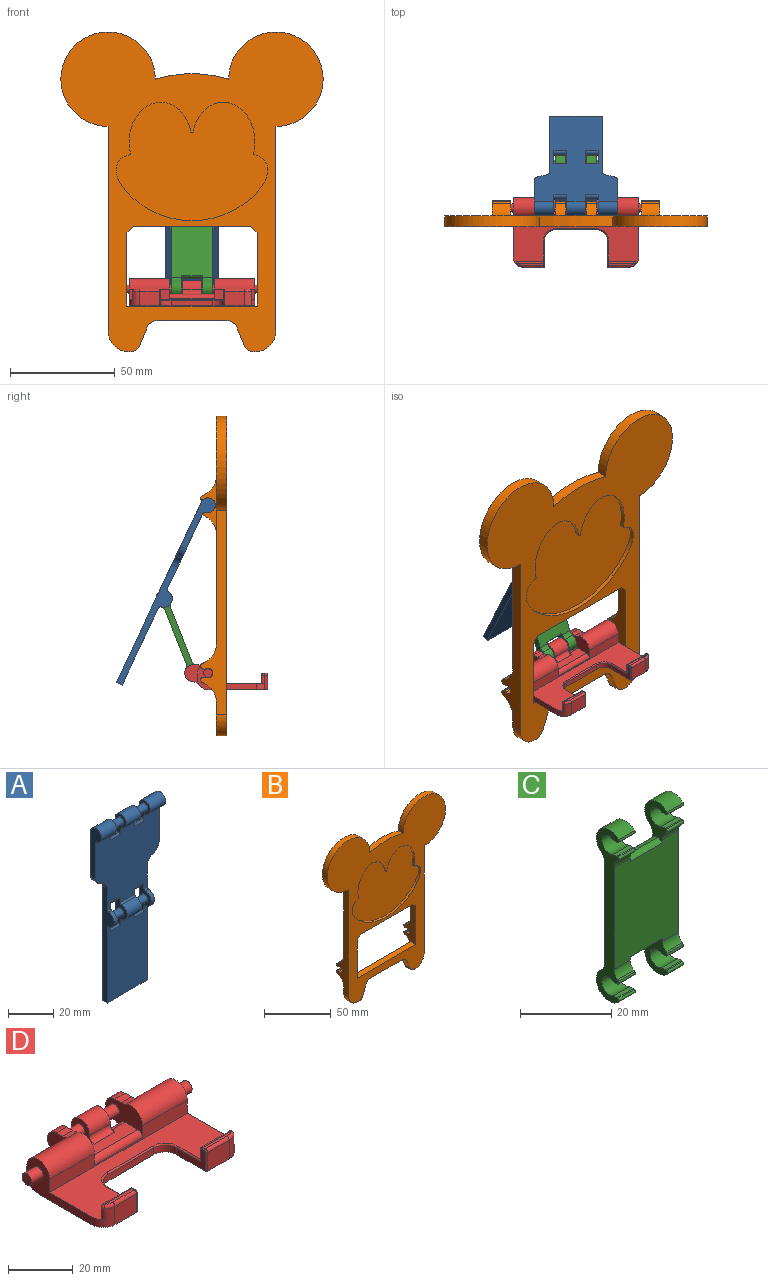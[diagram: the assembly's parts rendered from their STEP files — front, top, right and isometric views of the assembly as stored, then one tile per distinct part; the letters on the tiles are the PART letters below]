
ASSEMBLY  parts=4 mates=4
PART A: 57 faces, bbox 40x7.5x98.5 mm
  f0: cylinder r=4mm len=9mm, axis (-1,0,0), area 105.9mm2, adj f1,f2,f33,f40
  f1: cylinder r=1mm len=9mm, axis (-1,0,0), area 13.2mm2, adj f0,f12,f33,f40
  f2: cylinder r=1mm len=9mm, axis (-1,0,0), area 13.2mm2, adj f0,f9,f33,f40
  f3: plane 95x40mm, normal (0,1,0), area 2523.8mm2, adj f5,f11,f13,f14,f15,f16,f17,f18
  f4: cylinder r=2mm len=9mm, axis (-1,0,0), area 23.3mm2, adj f9,f11,f29,f36
  f5: cylinder r=3.5mm len=9.5mm, axis (-1,0,0), area 147.5mm2, adj f3,f14,f24,f35
  f6: cylinder r=4mm len=7.96mm, axis (-1,0,0), area 23.5mm2, adj f7,f8,f16,f39
  f7: cylinder r=1mm len=2mm, axis (-1,0,0), area 2.9mm2, adj f6,f12,f16,f39
  f8: cylinder r=1mm len=2mm, axis (-1,0,0), area 2.9mm2, adj f6,f9,f16,f39
  f9: plane 40x39.08mm, normal (0,-1,0), area 1254.7mm2, adj f2,f4,f8,f10,f14,f15,f16,f17
  f10: cylinder r=2mm len=9.5mm, axis (-1,0,0), area 24.6mm2, adj f9,f15,f22,f28
  f11: cylinder r=3.5mm len=9mm, axis (-1,0,0), area 139.7mm2, adj f3,f4,f29,f36
  f12: plane 40.68x25mm, normal (0,-1,0), area 982.3mm2, adj f1,f7,f13,f16,f18,f25,f32,f33
  f13: plane 25x3mm, normal (0,0,-1), area 75mm2, adj f3,f12,f16,f18
  f14: plane 26.82x7mm, normal (-1,0,0), area 101.1mm2, adj f3,f5,f9,f21,f24
  f15: plane 26.82x7mm, normal (1,0,0), area 101.1mm2, adj f3,f9,f10,f20,f22
  f16: plane 62x7.5mm, normal (-1,0,0), area 215.5mm2, adj f3,f6,f7,f8,f9,f12,f13,f17
  f17: cylinder r=5mm len=4.84mm, axis (0,1,0), area 19.8mm2, adj f3,f9,f16,f21
  f18: plane 62x7.5mm, normal (1,0,0), area 215.5mm2, adj f3,f9,f12,f13,f19,f23,f25,f26
  f19: cylinder r=5mm len=4.84mm, axis (0,1,0), area 19.8mm2, adj f3,f9,f18,f20
  f20: cylinder r=5mm len=4.84mm, axis (0,1,0), area 19.8mm2, adj f3,f9,f15,f19
  f21: cylinder r=5mm len=4.84mm, axis (0,1,0), area 19.8mm2, adj f3,f9,f14,f17
  f22: cylinder r=3.5mm len=9.5mm, axis (-1,0,0), area 147.5mm2, adj f3,f10,f15,f28
  f23: cylinder r=4mm len=7.96mm, axis (-1,0,0), area 23.5mm2, adj f18,f25,f26,f32
  f24: cylinder r=2mm len=9.5mm, axis (-1,0,0), area 24.6mm2, adj f5,f9,f14,f35
  f25: cylinder r=1mm len=2mm, axis (-1,0,0), area 2.9mm2, adj f12,f18,f23,f32
  f26: cylinder r=1mm len=2mm, axis (-1,0,0), area 2.9mm2, adj f9,f18,f23,f32
  f27: cylinder r=7mm len=6mm, axis (-1,0,0), area 5.4mm2, adj f28,f29,f55,f56
  f28: plane 11.36x7mm, normal (-1,0,0), area 39.2mm2, adj f3,f9,f10,f22,f27,f42,f55,f56
  f29: plane 11.36x7mm, normal (1,0,0), area 39.2mm2, adj f3,f4,f9,f11,f27,f42,f55,f56
  f30: cylinder r=7mm len=6mm, axis (-1,0,0), area 5.4mm2, adj f32,f33,f51,f53
  f31: cylinder r=7mm len=6mm, axis (-1,0,0), area 5.4mm2, adj f32,f33,f52,f54
  f32: plane 15.72x7.5mm, normal (-1,0,0), area 58.1mm2, adj f3,f9,f12,f23,f25,f26,f30,f31
  f33: plane 15.72x7.5mm, normal (1,0,0), area 58.1mm2, adj f0,f1,f2,f3,f9,f12,f30,f31
  f34: cylinder r=7mm len=6mm, axis (1,0,0), area 5.4mm2, adj f35,f36,f49,f50
  f35: plane 11.36x7mm, normal (1,0,0), area 39.2mm2, adj f3,f5,f9,f24,f34,f41,f49,f50
  f36: plane 11.36x7mm, normal (-1,0,0), area 39.2mm2, adj f3,f4,f9,f11,f34,f41,f49,f50
  f37: cylinder r=7mm len=6mm, axis (1,0,0), area 5.4mm2, adj f39,f40,f45,f47
  f38: cylinder r=7mm len=6mm, axis (1,0,0), area 5.4mm2, adj f39,f40,f46,f48
  f39: plane 15.72x7.5mm, normal (1,0,0), area 58.1mm2, adj f3,f6,f7,f8,f9,f12,f37,f38
  f40: plane 15.72x7.5mm, normal (-1,0,0), area 58.1mm2, adj f0,f1,f2,f3,f9,f12,f37,f38
  f41: cylinder r=2mm len=6mm, axis (-1,0,0), area 75.4mm2, adj f35,f36
  f42: cylinder r=2mm len=6mm, axis (-1,0,0), area 75.4mm2, adj f28,f29
  f43: cylinder r=2mm len=6mm, axis (-1,0,0), area 75.4mm2, adj f39,f40
  f44: cylinder r=2mm len=6mm, axis (-1,0,0), area 75.4mm2, adj f32,f33
  f45: cylinder r=1mm len=6mm, axis (1,0,0), area 8.3mm2, adj f9,f37,f39,f40
  f46: cylinder r=1mm len=6mm, axis (1,0,0), area 8.3mm2, adj f12,f38,f39,f40
  f47: cylinder r=1mm len=6mm, axis (1,0,0), area 11.3mm2, adj f3,f37,f39,f40
  f48: cylinder r=1mm len=6mm, axis (1,0,0), area 11.3mm2, adj f3,f38,f39,f40
  f49: cylinder r=1mm len=6mm, axis (1,0,0), area 8.3mm2, adj f9,f34,f35,f36
  f50: cylinder r=1mm len=6mm, axis (1,0,0), area 11.3mm2, adj f3,f34,f35,f36
  f51: cylinder r=1mm len=6mm, axis (-1,0,0), area 8.3mm2, adj f9,f30,f32,f33
  f52: cylinder r=1mm len=6mm, axis (-1,0,0), area 8.3mm2, adj f12,f31,f32,f33
  f53: cylinder r=1mm len=6mm, axis (-1,0,0), area 11.3mm2, adj f3,f30,f32,f33
  f54: cylinder r=1mm len=6mm, axis (-1,0,0), area 11.3mm2, adj f3,f31,f32,f33
  f55: cylinder r=1mm len=6mm, axis (-1,0,0), area 8.3mm2, adj f9,f27,f28,f29
  f56: cylinder r=1mm len=6mm, axis (-1,0,0), area 11.3mm2, adj f3,f27,f28,f29
PART B: 90 faces, bbox 125x12.5x152.5 mm
  f0: plane 80x21.9mm, normal (0,1,0), area 909.3mm2, adj f3,f7,f8,f9,f10,f11,f12,f13
  f1: plane 152.5x125mm, normal (0,-1,0), area 6689.7mm2, adj f3,f4,f5,f6,f7,f8,f9,f10
  f2: plane 125x108.48mm, normal (0,1,0), area 8063mm2, adj f4,f5,f6,f7,f9,f19,f20,f26
  f3: plane 5x0.45mm, normal (0,0,-1), area 2.2mm2, adj f0,f1,f10,f18
  f4: cylinder r=22.5mm len=45mm, axis (0,-1,0), area 530.1mm2, adj f1,f2,f5,f9
  f5: cylinder r=60mm len=35mm, axis (0,-1,0), area 177.6mm2, adj f1,f2,f4,f6
  f6: cylinder r=22.5mm len=45mm, axis (0,-1,0), area 530.1mm2, adj f1,f2,f5,f7
  f7: plane 97.5x12.49mm, normal (-1,0,0), area 566.5mm2, adj f0,f1,f2,f6,f10,f40,f41,f42
  f8: plane 5x0.45mm, normal (0,0,-1), area 2.2mm2, adj f0,f1,f11,f17
  f9: plane 97.5x12.49mm, normal (1,0,0), area 566.5mm2, adj f0,f1,f2,f4,f11,f27,f28,f29
  f10: cylinder r=10mm len=10mm, axis (0,-1,0), area 78.5mm2, adj f0,f1,f3,f7
  f11: cylinder r=10mm len=10mm, axis (0,1,0), area 78.5mm2, adj f0,f1,f8,f9
  f12: plane 33.32x5mm, normal (0,0,-1), area 166.6mm2, adj f0,f1,f15,f16
  f13: plane 8.83x5mm, normal (-0.92,0,-0.38), area 47.8mm2, adj f0,f1,f16,f17
  f14: plane 8.83x5mm, normal (0.92,0,-0.38), area 47.8mm2, adj f0,f1,f15,f18
  f15: cylinder r=5mm len=5mm, axis (0,1,0), area 29.5mm2, adj f0,f1,f12,f14
  f16: cylinder r=5mm len=5mm, axis (0,-1,0), area 29.5mm2, adj f0,f1,f12,f13
  f17: cylinder r=5mm len=5mm, axis (0,1,0), area 29.5mm2, adj f0,f1,f8,f13
  f18: cylinder r=5mm len=5mm, axis (0,-1,0), area 29.5mm2, adj f0,f1,f3,f14
  f19: plane 28.04x7.49mm, normal (1,0,0), area 79mm2, adj f2,f21,f22,f23,f24,f25,f53,f54
  f20: plane 28.04x7.49mm, normal (-1,0,0), area 79mm2, adj f2,f21,f22,f23,f24,f25,f53,f54
  f21: cylinder r=5.25mm len=5mm, axis (-1,0,0), area 4.5mm2, adj f19,f20,f56,f67
  f22: plane 5x0.31mm, normal (0,0,1), area 1.5mm2, adj f19,f20,f55,f77
  f23: cylinder r=2.3mm len=5mm, axis (-1,0,0), area 46.1mm2, adj f19,f20,f77,f78
  f24: plane 5x0.31mm, normal (0,0,-1), area 1.5mm2, adj f19,f20,f54,f78
  f25: cylinder r=5.25mm len=5mm, axis (-1,0,0), area 4.5mm2, adj f19,f20,f53,f68
  f26: plane 41.02x12.49mm, normal (-1,0,0), area 254.5mm2, adj f0,f1,f2,f27,f28,f29,f30,f31
  f27: cylinder r=5.25mm len=9mm, axis (-1,0,0), area 8mm2, adj f9,f26,f48,f65
  f28: plane 9x0.31mm, normal (0,0,1), area 2.8mm2, adj f9,f26,f47,f76
  f29: cylinder r=2.3mm len=9mm, axis (-1,0,0), area 83mm2, adj f9,f26,f75,f76
  f30: plane 9x0.31mm, normal (0,0,-1), area 2.8mm2, adj f9,f26,f46,f75
  f31: cylinder r=5.25mm len=9mm, axis (-1,0,0), area 8mm2, adj f9,f26,f45,f66
  f32: plane 28.04x7.49mm, normal (-1,0,0), area 79mm2, adj f2,f34,f35,f36,f37,f38,f57,f58
  f33: plane 28.04x7.49mm, normal (1,0,0), area 79mm2, adj f2,f34,f35,f36,f37,f38,f57,f58
  f34: cylinder r=5.25mm len=5mm, axis (1,0,0), area 4.5mm2, adj f32,f33,f58,f63
  f35: plane 5x0.31mm, normal (0,0,-1), area 1.5mm2, adj f32,f33,f57,f74
  f36: cylinder r=2.3mm len=5mm, axis (1,0,0), area 46.1mm2, adj f32,f33,f73,f74
  f37: plane 5x0.31mm, normal (0,0,1), area 1.5mm2, adj f32,f33,f60,f73
  f38: cylinder r=5.25mm len=5mm, axis (1,0,0), area 4.5mm2, adj f32,f33,f59,f64
  f39: plane 41.02x12.49mm, normal (1,0,0), area 254.5mm2, adj f0,f1,f2,f40,f41,f42,f43,f44
  f40: cylinder r=5.25mm len=9mm, axis (1,0,0), area 8mm2, adj f7,f39,f50,f61
  f41: plane 9x0.31mm, normal (0,0,-1), area 2.8mm2, adj f7,f39,f49,f71
  f42: cylinder r=2.3mm len=9mm, axis (1,0,0), area 83mm2, adj f7,f39,f71,f72
  f43: plane 9x0.31mm, normal (0,0,1), area 2.8mm2, adj f7,f39,f52,f72
  f44: cylinder r=5.25mm len=9mm, axis (1,0,0), area 8mm2, adj f7,f39,f51,f62
  f45: cylinder r=1.4mm len=9mm, axis (-1,0,0), area 17.3mm2, adj f9,f26,f31,f46
  f46: cylinder r=1.4mm len=9mm, axis (-1,0,0), area 14.4mm2, adj f9,f26,f30,f45
  f47: cylinder r=1.4mm len=9mm, axis (-1,0,0), area 14.4mm2, adj f9,f26,f28,f48
  f48: cylinder r=1.4mm len=9mm, axis (-1,0,0), area 17.3mm2, adj f9,f26,f27,f47
  f49: cylinder r=1.4mm len=9mm, axis (1,0,0), area 14.4mm2, adj f7,f39,f41,f50
  f50: cylinder r=1.4mm len=9mm, axis (1,0,0), area 17.3mm2, adj f7,f39,f40,f49
  f51: cylinder r=1.4mm len=9mm, axis (1,0,0), area 17.3mm2, adj f7,f39,f44,f52
  f52: cylinder r=1.4mm len=9mm, axis (1,0,0), area 14.4mm2, adj f7,f39,f43,f51
  f53: cylinder r=1.4mm len=5mm, axis (-1,0,0), area 9.6mm2, adj f19,f20,f25,f54
  f54: cylinder r=1.4mm len=5mm, axis (1,0,0), area 8mm2, adj f19,f20,f24,f53
  f55: cylinder r=1.4mm len=5mm, axis (-1,0,0), area 8mm2, adj f19,f20,f22,f56
  f56: cylinder r=1.4mm len=5mm, axis (-1,0,0), area 9.6mm2, adj f19,f20,f21,f55
  f57: cylinder r=1.4mm len=5mm, axis (-1,0,0), area 8mm2, adj f32,f33,f35,f58
  f58: cylinder r=1.4mm len=5mm, axis (1,0,0), area 9.6mm2, adj f32,f33,f34,f57
  f59: cylinder r=1.4mm len=5mm, axis (1,0,0), area 9.6mm2, adj f32,f33,f38,f60
  f60: cylinder r=1.4mm len=5mm, axis (1,0,0), area 8mm2, adj f32,f33,f37,f59
  f61: cylinder r=10mm len=9.19mm, axis (1,0,0), area 105mm2, adj f2,f7,f39,f40
  f62: cylinder r=10mm len=9.19mm, axis (1,0,0), area 105mm2, adj f0,f7,f39,f44
  f63: cylinder r=10mm len=9.19mm, axis (1,0,0), area 58.3mm2, adj f2,f32,f33,f34
  f64: cylinder r=10mm len=9.19mm, axis (1,0,0), area 58.3mm2, adj f2,f32,f33,f38
  f65: cylinder r=10mm len=9.19mm, axis (-1,0,0), area 105mm2, adj f0,f9,f26,f27
  f66: cylinder r=10mm len=9.19mm, axis (-1,0,0), area 105mm2, adj f2,f9,f26,f31
  f67: cylinder r=10mm len=9.19mm, axis (-1,0,0), area 58.3mm2, adj f2,f19,f20,f21
  f68: cylinder r=10mm len=9.19mm, axis (-1,0,0), area 58.3mm2, adj f2,f19,f20,f25
  f69: plane 56x5mm, normal (0,0,-1), area 280mm2, adj f1,f2,f79,f80
  f70: plane 62x5mm, normal (0,0,1), area 310mm2, adj f0,f1,f26,f39
  f71: cylinder r=2mm len=9mm, axis (1,0,0), area 7.8mm2, adj f7,f39,f41,f42
  f72: cylinder r=2mm len=9mm, axis (1,0,0), area 7.8mm2, adj f7,f39,f42,f43
  f73: cylinder r=2mm len=5mm, axis (1,0,0), area 4.3mm2, adj f32,f33,f36,f37
  f74: cylinder r=2mm len=5mm, axis (1,0,0), area 4.3mm2, adj f32,f33,f35,f36
  f75: cylinder r=2mm len=9mm, axis (-1,0,0), area 7.8mm2, adj f9,f26,f29,f30
  f76: cylinder r=2mm len=9mm, axis (-1,0,0), area 7.8mm2, adj f9,f26,f28,f29
  f77: cylinder r=2mm len=5mm, axis (-1,0,0), area 4.3mm2, adj f19,f20,f22,f23
  f78: cylinder r=2mm len=5mm, axis (-1,0,0), area 4.3mm2, adj f19,f20,f23,f24
  f79: plane 5x3mm, normal (-0.71,0,-0.71), area 21.2mm2, adj f1,f2,f26,f69
  f80: plane 5x3mm, normal (0.71,0,-0.71), area 21.2mm2, adj f1,f2,f39,f69
  f81: extruded ~29.51x24.32mm, area 108.2mm2, adj f1,f86,f87,f88
  f82: extruded ~24.78x13.29mm, area 66.6mm2, adj f1,f83,f86,f88
  f83: cylinder r=42.28mm len=45.75mm, axis (0,-1,0), area 96.7mm2, adj f1,f82,f84,f86
  f84: extruded ~24.78x13.29mm, area 66.6mm2, adj f1,f83,f86,f89
  f85: extruded ~29.51x24.32mm, area 108.2mm2, adj f1,f86,f87,f89
  f86: plane 72.34x56.42mm, normal (0,-1,0), area 3067.8mm2, adj f81,f82,f83,f84,f85,f87,f88,f89
  f87: cylinder r=0.5mm len=2mm, axis (0,-1,0), area 2.7mm2, adj f1,f81,f85,f86
  f88: cylinder r=0.5mm len=2mm, axis (0,-1,0), area 1.5mm2, adj f1,f81,f82,f86
  f89: cylinder r=0.5mm len=2mm, axis (0,-1,0), area 1.5mm2, adj f1,f84,f85,f86
PART C: 56 faces, bbox 20x7x46 mm
  f0: cylinder r=3mm len=5mm, axis (-1,0,0), area 13.1mm2, adj f4,f7,f13,f17
  f1: cylinder r=3mm len=5mm, axis (-1,0,0), area 13.1mm2, adj f5,f7,f11,f16
  f2: cylinder r=3mm len=5mm, axis (-1,0,0), area 13.1mm2, adj f6,f10,f17,f19
  f3: cylinder r=3mm len=5mm, axis (-1,0,0), area 13.1mm2, adj f6,f12,f16,f18
  f4: cylinder r=4mm len=7.06mm, axis (-1,0,0), area 65mm2, adj f0,f7,f13,f41
  f5: cylinder r=4mm len=5mm, axis (-1,0,0), area 2.1mm2, adj f1,f7,f11,f44
  f6: plane 46x7.02mm, normal (1,0,0), area 144.3mm2, adj f2,f3,f8,f9,f16,f17,f18,f19
  f7: plane 46x7.02mm, normal (-1,0,0), area 144.3mm2, adj f0,f1,f4,f5,f14,f15,f16,f17
  f8: cylinder r=4mm len=7.06mm, axis (-1,0,0), area 65mm2, adj f6,f12,f42,f48
  f9: cylinder r=4mm len=5mm, axis (-1,0,0), area 2.1mm2, adj f6,f10,f46,f49
  f10: plane 10.2x7.02mm, normal (-1,0,0), area 32.3mm2, adj f2,f9,f16,f17,f19,f29,f30,f31
  f11: plane 10.2x7.02mm, normal (1,0,0), area 32.3mm2, adj f1,f5,f15,f16,f17,f26,f27,f28
  f12: plane 10.2x7.02mm, normal (-1,0,0), area 32.3mm2, adj f3,f8,f16,f17,f18,f23,f24,f25
  f13: plane 10.2x7.02mm, normal (1,0,0), area 32.3mm2, adj f0,f4,f14,f16,f17,f20,f21,f22
  f14: cylinder r=4mm len=5mm, axis (-1,0,0), area 2.1mm2, adj f7,f13,f40,f51
  f15: cylinder r=4mm len=7.06mm, axis (-1,0,0), area 65mm2, adj f7,f11,f45,f50
  f16: plane 27.28x20mm, normal (0,-1,0), area 528.8mm2, adj f1,f3,f6,f7,f10,f11,f12,f13
  f17: plane 27.28x20mm, normal (0,1,0), area 528.8mm2, adj f0,f2,f6,f7,f10,f11,f12,f13
  f18: cylinder r=4mm len=5mm, axis (-1,0,0), area 2.1mm2, adj f3,f6,f12,f43
  f19: cylinder r=4mm len=7.06mm, axis (-1,0,0), area 65mm2, adj f2,f6,f10,f47
  f20: plane 5x1.07mm, normal (0,0,1), area 5.4mm2, adj f7,f13,f22,f32
  f21: plane 5x1.07mm, normal (0,0,-1), area 5.4mm2, adj f7,f13,f22,f33
  f22: cylinder r=2.3mm len=5mm, axis (-1,0,0), area 49.9mm2, adj f7,f13,f20,f21
  f23: cylinder r=2.3mm len=5mm, axis (-1,0,0), area 49.9mm2, adj f6,f12,f24,f25
  f24: plane 5x1.07mm, normal (0,0,-1), area 5.4mm2, adj f6,f12,f23,f34
  f25: plane 5x1.07mm, normal (0,0,1), area 5.4mm2, adj f6,f12,f23,f35
  f26: plane 5x1.07mm, normal (0,0,1), area 5.4mm2, adj f7,f11,f28,f37
  f27: plane 5x1.07mm, normal (0,0,-1), area 5.4mm2, adj f7,f11,f28,f36
  f28: cylinder r=2.3mm len=5mm, axis (-1,0,0), area 49.9mm2, adj f7,f11,f26,f27
  f29: cylinder r=2.3mm len=5mm, axis (-1,0,0), area 49.9mm2, adj f6,f10,f30,f31
  f30: plane 5x1.07mm, normal (0,0,-1), area 5.4mm2, adj f6,f10,f29,f38
  f31: plane 5x1.07mm, normal (0,0,1), area 5.4mm2, adj f6,f10,f29,f39
  f32: cylinder r=1mm len=5mm, axis (-1,0,0), area 1.6mm2, adj f7,f13,f20,f40
  f33: cylinder r=1mm len=5mm, axis (-1,0,0), area 1.6mm2, adj f7,f13,f21,f41
  f34: cylinder r=1mm len=5mm, axis (-1,0,0), area 1.6mm2, adj f6,f12,f24,f42
  f35: cylinder r=1mm len=5mm, axis (-1,0,0), area 1.6mm2, adj f6,f12,f25,f43
  f36: cylinder r=1mm len=5mm, axis (-1,0,0), area 1.6mm2, adj f7,f11,f27,f44
  f37: cylinder r=1mm len=5mm, axis (-1,0,0), area 1.6mm2, adj f7,f11,f26,f45
  f38: cylinder r=1mm len=5mm, axis (-1,0,0), area 1.6mm2, adj f6,f10,f30,f46
  f39: cylinder r=1mm len=5mm, axis (-1,0,0), area 1.6mm2, adj f6,f10,f31,f47
  f40: cylinder r=0.5mm len=5mm, axis (-1,0,0), area 5mm2, adj f7,f13,f14,f32
  f41: cylinder r=0.5mm len=5mm, axis (1,0,0), area 5mm2, adj f4,f7,f13,f33
  f42: cylinder r=0.5mm len=5mm, axis (1,0,0), area 5mm2, adj f6,f8,f12,f34
  f43: cylinder r=0.5mm len=5mm, axis (-1,0,0), area 5mm2, adj f6,f12,f18,f35
  f44: cylinder r=0.5mm len=5mm, axis (1,0,0), area 5mm2, adj f5,f7,f11,f36
  f45: cylinder r=0.5mm len=5mm, axis (-1,0,0), area 5mm2, adj f7,f11,f15,f37
  f46: cylinder r=0.5mm len=5mm, axis (1,0,0), area 5mm2, adj f6,f9,f10,f38
  f47: cylinder r=0.5mm len=5mm, axis (-1,0,0), area 5mm2, adj f6,f10,f19,f39
  f48: cylinder r=3mm len=5mm, axis (-1,0,0), area 13.1mm2, adj f6,f8,f12,f17
  f49: cylinder r=3mm len=5mm, axis (-1,0,0), area 13.1mm2, adj f6,f9,f10,f16
  f50: cylinder r=3mm len=5mm, axis (-1,0,0), area 13.1mm2, adj f7,f11,f15,f17
  f51: cylinder r=3mm len=5mm, axis (-1,0,0), area 13.1mm2, adj f7,f13,f14,f16
  f52: cylinder r=2mm len=10mm, axis (-1,0,0), area 17.1mm2, adj f12,f13,f17,f53
  f53: cylinder r=2mm len=10mm, axis (1,0,0), area 17.1mm2, adj f12,f13,f16,f52
  f54: cylinder r=2mm len=10mm, axis (-1,0,0), area 17.1mm2, adj f10,f11,f16,f55
  f55: cylinder r=2mm len=10mm, axis (1,0,0), area 17.1mm2, adj f10,f11,f17,f54
PART D: 79 faces, bbox 70x39.9x13 mm
  f0: plane 60x22.15mm, normal (0,0,1), area 757.9mm2, adj f8,f9,f10,f43,f44,f46,f48,f50
  f1: plane 9.43x7mm, normal (0,-1,0), area 66mm2, adj f5,f50,f63,f78
  f2: cylinder r=2mm len=6mm, axis (-1,0,0), area 75.4mm2, adj f19,f28
  f3: cylinder r=5mm len=19.5mm, axis (-1,0,0), area 281.1mm2, adj f4,f8,f10,f14,f15,f42
  f4: plane 15x3mm, normal (0,1,0), area 45mm2, adj f3,f8,f14,f20
  f5: plane 60x28.4mm, normal (0,0,-1), area 1163.5mm2, adj f1,f7,f8,f9,f20,f34,f35,f36
  f6: plane 15x3mm, normal (0,1,0), area 45mm2, adj f9,f11,f18,f20
  f7: plane 9.43x7mm, normal (0,-1,0), area 66mm2, adj f5,f53,f59,f64
  f8: plane 28.33x13mm, normal (1,0,0), area 155mm2, adj f0,f3,f4,f5,f10,f20,f23,f52
  f9: plane 28.33x13mm, normal (-1,0,0), area 155mm2, adj f0,f5,f6,f10,f11,f20,f25,f51
  f10: plane 60x5mm, normal (0,-1,0), area 205.5mm2, adj f0,f3,f8,f9,f11,f15,f19,f45
  f11: cylinder r=5mm len=19.5mm, axis (-1,0,0), area 281.1mm2, adj f6,f9,f10,f18,f19,f41
  f12: plane 4.5x2.74mm, normal (0,0,1), area 12.3mm2, adj f13,f14,f15,f42
  f13: cylinder r=4mm len=7.96mm, axis (-1,0,0), area 53.9mm2, adj f12,f14,f15,f33
  f14: plane 10.63x8.92mm, normal (1,0,0), area 46mm2, adj f3,f4,f12,f13,f20,f33,f42
  f15: plane 16.1x11.13mm, normal (-1,0,0), area 100.1mm2, adj f3,f10,f12,f13,f20,f21,f26,f33
  f16: plane 4.5x2.74mm, normal (0,0,1), area 12.3mm2, adj f17,f18,f19,f41
  f17: cylinder r=4mm len=7.96mm, axis (1,0,0), area 53.9mm2, adj f16,f18,f19,f32
  f18: plane 10.63x8.92mm, normal (-1,0,0), area 46mm2, adj f6,f11,f16,f17,f20,f32,f41
  f19: plane 16.1x11.13mm, normal (1,0,0), area 100.1mm2, adj f2,f10,f11,f16,f17,f20,f21,f32
  f20: cylinder r=5mm len=60mm, axis (1,0,0), area 378.9mm2, adj f4,f5,f6,f8,f9,f14,f15,f18
  f21: plane 21x5.6mm, normal (0,0,1), area 104.3mm2, adj f15,f19,f27,f28,f30,f39,f40,f45
  f22: plane 4.2x4.2mm, normal (1,0,0), area 13.9mm2, adj f23
  f23: cylinder r=2.1mm len=5mm, axis (-1,0,0), area 66mm2, adj f8,f22
  f24: plane 4.2x4.2mm, normal (-1,0,0), area 13.9mm2, adj f25
  f25: cylinder r=2.1mm len=5mm, axis (1,0,0), area 66mm2, adj f9,f24
  f26: cylinder r=2mm len=6mm, axis (-1,0,0), area 75.4mm2, adj f15,f27
  f27: plane 10.13x9.98mm, normal (1,0,0), area 42.2mm2, adj f20,f21,f26,f29,f30,f31,f40
  f28: plane 10.13x9.98mm, normal (-1,0,0), area 42.2mm2, adj f2,f20,f21,f29,f30,f31,f39
  f29: cylinder r=4mm len=9mm, axis (-1,0,0), area 167.3mm2, adj f27,f28,f30,f31
  f30: cylinder r=2mm len=9mm, axis (-1,0,0), area 29.8mm2, adj f21,f27,f28,f29
  f31: cylinder r=6mm len=9mm, axis (-1,0,0), area 40.3mm2, adj f20,f27,f28,f29
  f32: cylinder r=6mm len=4.5mm, axis (1,0,0), area 20.1mm2, adj f17,f18,f19,f20
  f33: cylinder r=6mm len=4.5mm, axis (1,0,0), area 20.1mm2, adj f13,f14,f15,f20
  f34: plane 20x2.5mm, normal (0,-1,0), area 50mm2, adj f5,f37,f38,f71
  f35: plane 12.5x7.5mm, normal (1,0,0), area 41.1mm2, adj f5,f37,f73,f74,f75,f76,f77,f78
  f36: plane 12.5x7.5mm, normal (-1,0,0), area 41.1mm2, adj f5,f38,f64,f65,f66,f67,f68,f69
  f37: cylinder r=5mm len=5mm, axis (0,0,1), area 19.6mm2, adj f5,f34,f35,f72
  f38: cylinder r=5mm len=5mm, axis (0,0,-1), area 19.6mm2, adj f5,f34,f36,f70
  f39: cylinder r=2mm len=6mm, axis (1,0,0), area 25.1mm2, adj f19,f20,f21,f28
  f40: cylinder r=2mm len=6mm, axis (1,0,0), area 25.1mm2, adj f15,f20,f21,f27
  f41: cylinder r=5mm len=4.5mm, axis (-1,0,0), area 10.1mm2, adj f11,f16,f18,f19
  f42: cylinder r=5mm len=4.5mm, axis (-1,0,0), area 10.1mm2, adj f3,f12,f14,f15
  f43: plane 3x0.07mm, normal (0.71,-0.71,0), area 0.3mm2, adj f0,f5,f52,f53
  f44: plane 3x0.07mm, normal (-0.71,-0.71,0), area 0.3mm2, adj f0,f5,f50,f51
  f45: cylinder r=2mm len=21mm, axis (-1,0,0), area 66mm2, adj f10,f15,f19,f21
  f46: plane 12.07x4mm, normal (0,1,0), area 48.3mm2, adj f0,f55,f60,f74
  f47: plane 12.07x1mm, normal (0,0,1), area 11.2mm2, adj f55,f62,f63,f76
  f48: plane 12.07x4mm, normal (0,1,0), area 48.3mm2, adj f0,f54,f56,f68
  f49: plane 12.07x1mm, normal (0,0,1), area 11.2mm2, adj f54,f58,f59,f66
  f50: cylinder r=5mm len=7mm, axis (0,0,-1), area 26.2mm2, adj f0,f1,f5,f44,f60,f62
  f51: cylinder r=5mm len=3.54mm, axis (0,0,-1), area 11.8mm2, adj f0,f5,f9,f44
  f52: cylinder r=5mm len=3.54mm, axis (0,0,1), area 11.8mm2, adj f0,f5,f8,f43
  f53: cylinder r=5mm len=7mm, axis (0,0,-1), area 26.2mm2, adj f0,f5,f7,f43,f56,f58
  f54: cylinder r=1mm len=12.07mm, axis (1,0,0), area 19mm2, adj f48,f49,f57,f67
  f55: cylinder r=1mm len=12.07mm, axis (1,0,0), area 19mm2, adj f46,f47,f61,f75
  f56: cylinder r=1mm len=4mm, axis (0,0,-1), area 9.7mm2, adj f0,f48,f53,f57
  f57: sphere r=1mm, area 2.4mm2, adj f54,f56,f58
  f58: torus R=4mm, axis (0,0,1), area 5.3mm2, adj f49,f53,f57,f59
  f59: cylinder r=1mm len=9.43mm, axis (-1,0,0), area 14.8mm2, adj f7,f49,f58,f65
  f60: cylinder r=1mm len=4mm, axis (0,0,-1), area 9.7mm2, adj f0,f46,f50,f61
  f61: sphere r=1mm, area 2.4mm2, adj f55,f60,f62
  f62: torus R=4mm, axis (0,0,1), area 5.3mm2, adj f47,f50,f61,f63
  f63: cylinder r=1mm len=9.43mm, axis (-1,0,0), area 14.8mm2, adj f1,f47,f62,f77
  f64: cylinder r=0.5mm len=7mm, axis (0,0,1), area 5.5mm2, adj f5,f7,f36,f65
  f65: torus R=0.5mm, axis (-1,0,0), area 1mm2, adj f36,f59,f64,f66
  f66: cylinder r=0.5mm len=1mm, axis (0,-1,0), area 0.8mm2, adj f36,f49,f65,f67
  f67: torus R=0.5mm, axis (-1,0,0), area 1mm2, adj f36,f54,f66,f68
  f68: cylinder r=0.5mm len=4.5mm, axis (0,0,-1), area 3.3mm2, adj f36,f48,f67,f69
  f69: cylinder r=0.5mm len=10.5mm, axis (0,1,0), area 8mm2, adj f0,f36,f68,f70
  f70: torus R=5.5mm, axis (0,0,-1), area 6.4mm2, adj f0,f38,f69,f71
  f71: cylinder r=0.5mm len=20mm, axis (-1,0,0), area 15.7mm2, adj f0,f34,f70,f72
  f72: torus R=5.5mm, axis (0,0,-1), area 6.4mm2, adj f0,f37,f71,f73
  f73: cylinder r=0.5mm len=10.5mm, axis (0,-1,0), area 8mm2, adj f0,f35,f72,f74
  f74: cylinder r=0.5mm len=4.5mm, axis (0,0,-1), area 3.3mm2, adj f35,f46,f73,f75
  f75: torus R=0.5mm, axis (-1,0,0), area 1mm2, adj f35,f55,f74,f76
  f76: cylinder r=0.5mm len=1mm, axis (0,1,0), area 0.8mm2, adj f35,f47,f75,f77
  f77: torus R=0.5mm, axis (-1,0,0), area 1mm2, adj f35,f63,f76,f78
  f78: cylinder r=0.5mm len=7mm, axis (0,0,-1), area 5.5mm2, adj f1,f5,f35,f77
PLACE A rot(axis=(1,0,0),25.2deg) t=(0,12.17,89.59)mm
PLACE B t=(0,0,8.1)mm
PLACE C rot(axis=(1,0,0),158.5deg) t=(0,23.06,25.78)mm
PLACE D rot(axis=(0.99,-0.06,0.12),0deg) t=(0,9.1,0.1)mm
MATE revolute A.f41 <-> B.f21  axis (-1,0,0) through (7.5,9,88.1)mm
MATE revolute D.f2 <-> C.f22  axis (-1,0,0) through (7.5,16.1,8.1)mm
MATE revolute C.f28 <-> A.f0  axis (-1,0,0) through (7.5,30.03,43.45)mm
MATE revolute D.f3 <-> B.f27  axis (-1,0,0) through (32.5,9,8.1)mm
